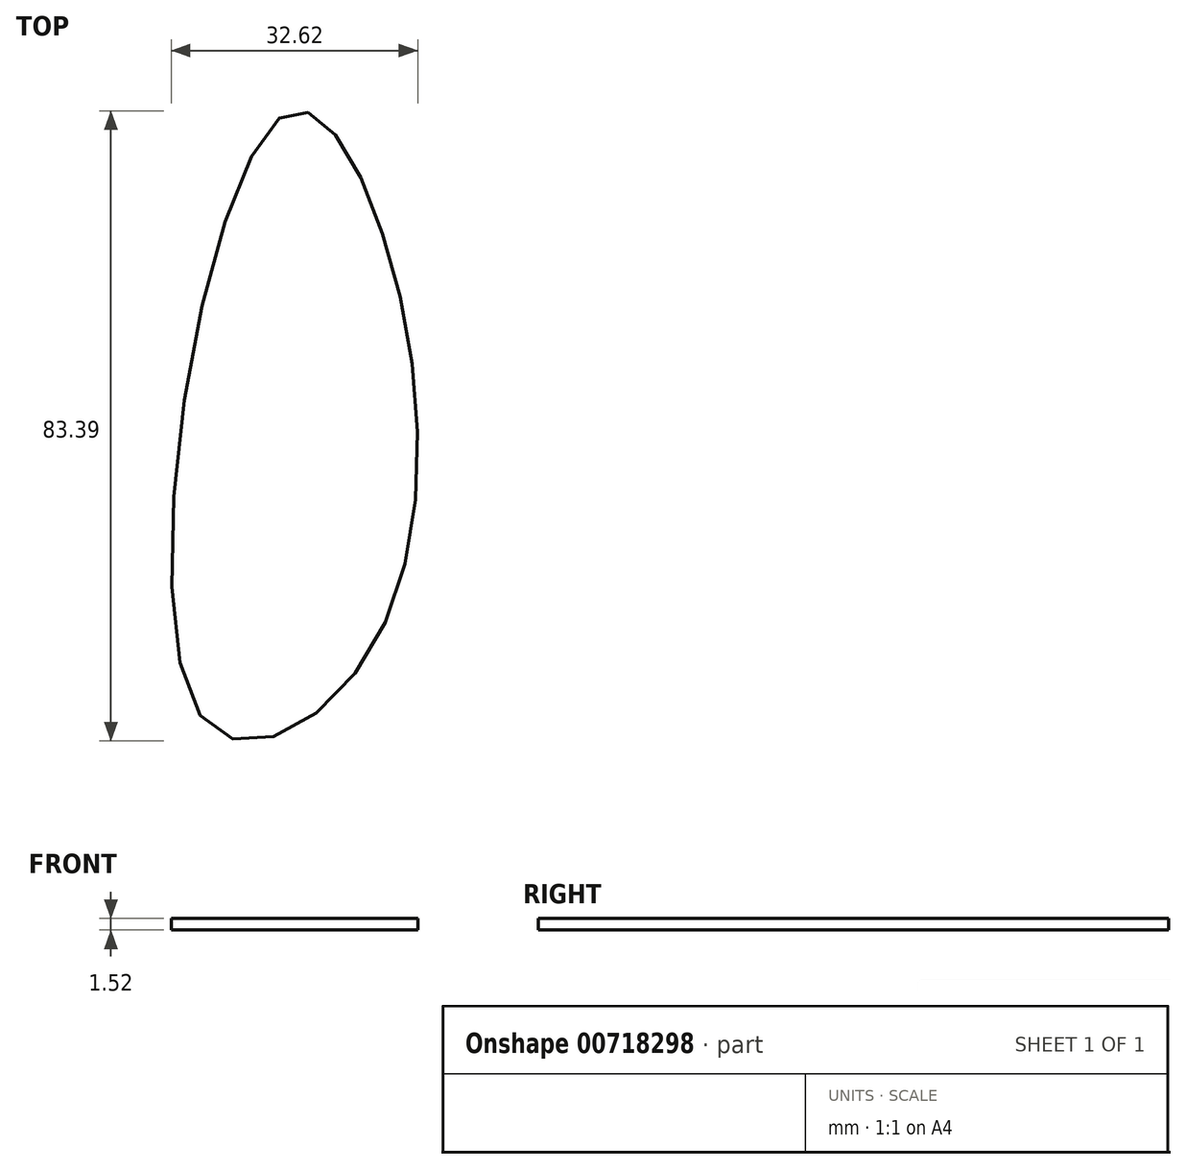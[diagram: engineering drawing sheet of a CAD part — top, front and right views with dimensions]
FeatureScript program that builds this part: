
annotation { "Feature Type Name" : "Feature", "Feature Type Description" : "" }
export const myFeature = defineFeature(function(context is Context, id is Id, definition is map)
    precondition{}
    {
        {
            var Q0;
            Q0=qCreatedBy(makeId("Top.planeOp"),FACE);
            var sketch = newSketch(context, id + "F0", { "sketchPlane" : qUnion([Q0])});
            skFitSpline(sketch, "E0", {"points": [v(0, 0) * mm, v(21.8, 7.37) * mm, v(24.21, 63.62) * mm, v(10.38, 78.96) * mm, v(0, 0) * mm]});
            skSolve(sketch);
        }
        {
            var Q0;
            Q0 = qSketchRegion(id + "F0", true);
            extrude(context, id + "F1", {"entities" : qUnion([Q0]), "oppositeDirection" : true, "depth" : 1.52 * mm, "offsetDistance" : 25.4 * mm});
        }
    });
